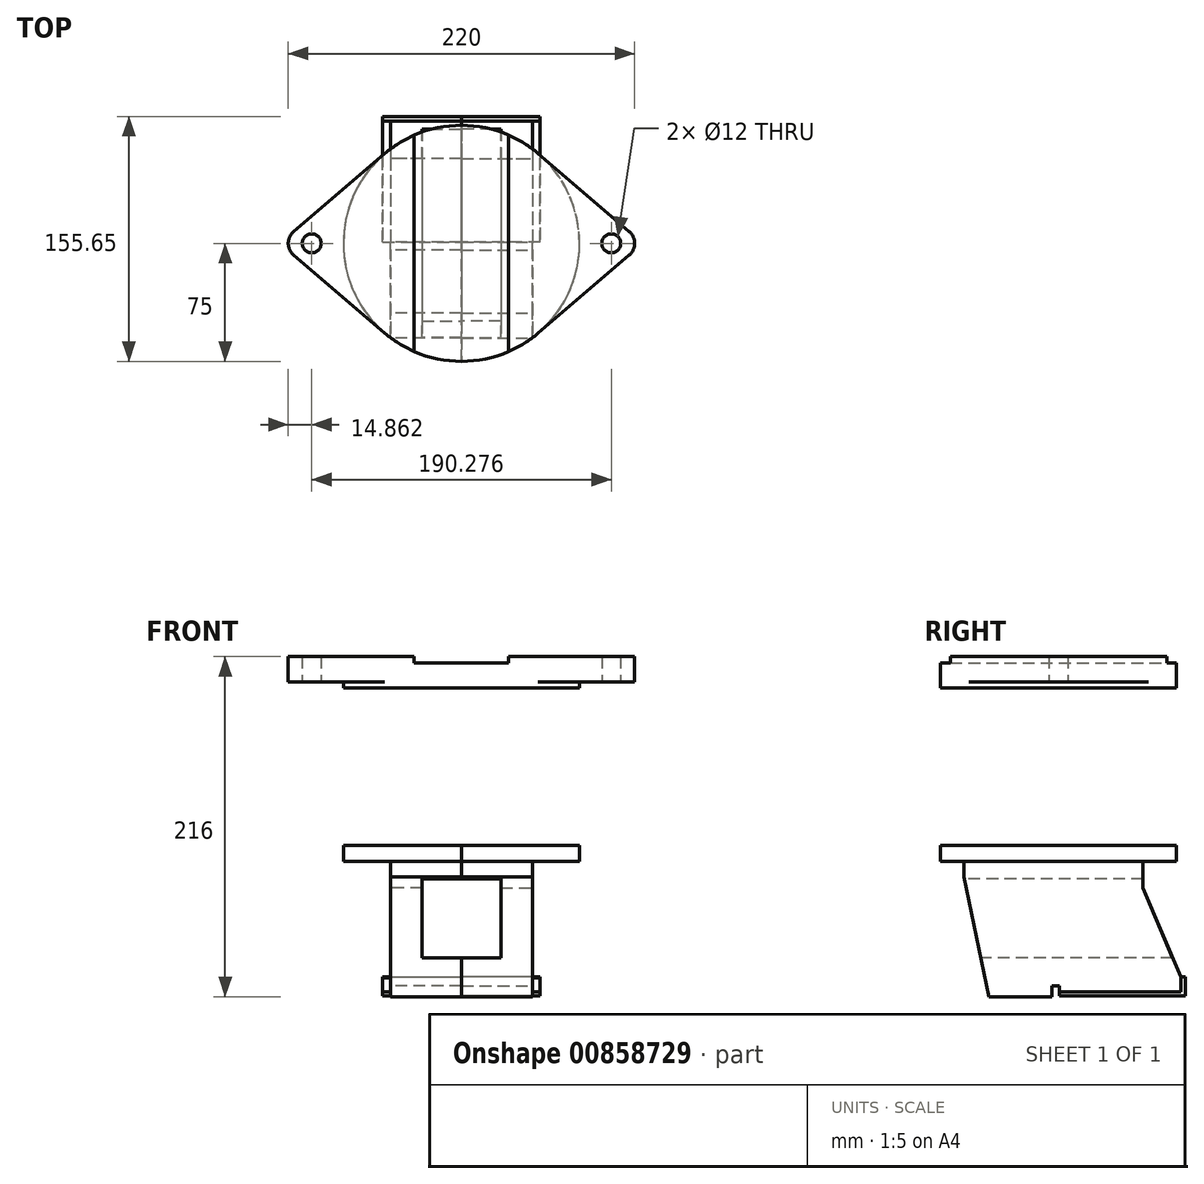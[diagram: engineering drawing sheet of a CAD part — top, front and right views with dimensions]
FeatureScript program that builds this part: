
annotation { "Feature Type Name" : "Feature", "Feature Type Description" : "" }
export const myFeature = defineFeature(function(context is Context, id is Id, definition is map)
    precondition{}
    {
        {
            var Q0;
            Q0=qCreatedBy(makeId("Top.planeOp"),FACE);
            var sketch = newSketch(context, id + "F0", { "sketchPlane" : qUnion([Q0])});
            skArc(sketch, "E0", {"start": v(0, 75) * mm, "mid": v(-25.99, 70.35) * mm, "end": v(-48.75, 57) * mm});
            skLineSegment(sketch, "E1", {"start": v(0, 0) * mm, "end": v(0, 0) * mm});
            skArc(sketch, "E2", {"start": v(-106.5, 7.6) * mm, "mid": v(-110, 0) * mm, "end": v(-106.5, -7.6) * mm});
            skLineSegment(sketch, "E3", {"start": v(-106.5, -7.6) * mm, "end": v(-48.75, -57) * mm});
            skLineSegment(sketch, "E4", {"start": v(-48.75, 57) * mm, "end": v(-106.5, 7.6) * mm});
            skArc(sketch, "E5.trimOffspring", {"start": v(-48.75, -57) * mm, "mid": v(-25.99, -70.35) * mm, "end": v(0, -75) * mm});
            skArc(sketch, "E6", {"start": v(0, 75) * mm, "mid": v(-75, 0) * mm, "end": v(0, -75) * mm});
            skLineSegment(sketch, "E7", {"start": v(0, 104.02) * mm, "end": v(0, -91.19) * mm});
            skSolve(sketch);
        }
        {
            var Q0;
            Q0=makeQuery(id+"F0.imprint","IMPRINT",FACE,{"disambiguationData":[TD([[makeQuery(id+"F0.imprint","IMPRINT",EDGE,{"derivedFrom":sQuery(id+"F0.wireOp",EDGE,"E2")}),1.0]])]});
            extrude(context, id + "F1", {"entities" : qUnion([Q0]), "oppositeDirection" : true, "depth" : 16 * mm, "offsetDistance" : 25 * mm});
        }
        {
            var Q0;
            {var subQ0=sQuery(id+"F0.wireOp",EDGE,"E6");var subQ1=makeQuery(id+"F0.imprint","INTERSECT",VERTEX,{"derivedFrom":[sQuery(id+"F0.wireOp",EDGE,"E4"),subQ0]});Q0=makeQuery(id+"F0.imprint","IMPRINT",FACE,{"disambiguationData":[TD([[makeQuery(id+"F0.imprint","IMPRINT",EDGE,{"disambiguationData":[TD([[subQ1,1.0]])],"derivedFrom":subQ0}),1.0]])]});}
            extrude(context, id + "F2", {"entities" : qUnion([Q0]), "oppositeDirection" : true, "depth" : 20 * mm, "offsetDistance" : 25 * mm});
        }
        {
            var Q0;
            Q0=makeQuery(id+"F1.opExtrude","CAP_FACE",FACE,{"disambiguationData":[OSD([sQuery(id+"F0.wireOp",EDGE,"E2"),sQuery(id+"F0.wireOp",EDGE,"E3"),sQuery(id+"F0.wireOp",EDGE,"E4"),sQuery(id+"F0.wireOp",EDGE,"E6")])],"isStart":false});
            var sketch = newSketch(context, id + "F3", { "sketchPlane" : qUnion([Q0])});
            skCircle(sketch, "E8", {"center": v(-95.14, 0) * mm, "radius": 6 * mm});
            skSolve(sketch);
        }
        {
            var Q0;
            Q0=makeQuery(id+"F3.imprint","IMPRINT",FACE,{"disambiguationData":[TD([[makeQuery(id+"F3.imprint","IMPRINT",EDGE,{"derivedFrom":sQuery(id+"F3.wireOp",EDGE,"E8")}),1.0]])]});
            extrude(context, id + "F4", {"entities" : qUnion([Q0]), "operationType" : NewBodyOperationType.REMOVE, "oppositeDirection" : true, "depth" : 16 * mm, "offsetDistance" : 25 * mm});
        }
        {
            var Q0;
            Q0=qCreatedBy(makeId("Front.planeOp"),FACE);
            var sketch = newSketch(context, id + "F5", { "sketchPlane" : qUnion([Q0])});
            skLineSegment(sketch, "E9", {"start": v(0, 0) * mm, "end": v(-30, 0) * mm});
            skLineSegment(sketch, "E10", {"start": v(-30, 0) * mm, "end": v(-30, -4) * mm});
            skLineSegment(sketch, "E11", {"start": v(-30, -4) * mm, "end": v(0, -4) * mm});
            skLineSegment(sketch, "E12", {"start": v(0, -4) * mm, "end": v(0, 0) * mm});
            skSolve(sketch);
        }
        {
            var Q0;
            Q0 = qSketchRegion(id + "F5", true);
            extrude(context, id + "F6", {"entities" : qUnion([Q0]), "operationType" : NewBodyOperationType.REMOVE, "endBound" : BoundingType.SYMMETRIC, "depth" : 150 * mm, "offsetDistance" : 25 * mm});
        }
        {
            var Q0;
            Q0=makeQuery(id+"F1.opExtrude","SWEPT_BODY",BODY,{"disambiguationData":[OSD([sQuery(id+"F0.wireOp",EDGE,"E2"),sQuery(id+"F0.wireOp",EDGE,"E3"),sQuery(id+"F0.wireOp",EDGE,"E4"),sQuery(id+"F0.wireOp",EDGE,"E6")])]});
            var Q1;
            Q1=makeQuery(id+"F2.opExtrude","SWEPT_BODY",BODY,{"disambiguationData":[OSD([sQuery(id+"F0.wireOp",EDGE,"E6"),sQuery(id+"F0.wireOp",EDGE,"E7")])]});
            var Q2;
            Q2=makeQuery(id+"F2.opExtrude","SWEPT_FACE",FACE,{"disambiguationData":[OSD([sQuery(id+"F0.wireOp",EDGE,"E7")])]});
            mirror(context, id + "F7", {"operationType" : NewBodyOperationType.ADD, "entities" : qUnion([Q0, Q1]), "mirrorPlane" : qUnion([Q2])});
        }
        {
            var Q0;
            {var subQ0=makeQuery(id+"F2.opExtrude","CAP_FACE",FACE,{"disambiguationData":[OSD([sQuery(id+"F0.wireOp",EDGE,"E6"),sQuery(id+"F0.wireOp",EDGE,"E7")])],"isStart":false});Q0=makeQuery(id+"F7.boolean.opBoolean","MERGE",FACE,{"derivedFrom":[subQ0,makeQuery(id+"F7.opPattern","COPY",FACE,{"derivedFrom":subQ0,"instanceName":"1"})]});}
            var sketch = newSketch(context, id + "F8", { "sketchPlane" : qUnion([Q0])});
            skCircle(sketch, "E13", {"center": v(0, 0) * mm, "radius": 75 * mm});
            skSolve(sketch);
        }
        {
            var Q0;
            Q0 = qSketchRegion(id + "F8", true);
            var Q1;
            {var subQ0=makeQuery(id+"F2.opExtrude","CAP_FACE",FACE,{"disambiguationData":[OSD([sQuery(id+"F0.wireOp",EDGE,"E6"),sQuery(id+"F0.wireOp",EDGE,"E7")])],"isStart":false});Q1=makeQuery(id+"F7.boolean.opBoolean","MERGE",FACE,{"derivedFrom":[subQ0,makeQuery(id+"F7.opPattern","COPY",FACE,{"derivedFrom":subQ0,"instanceName":"1"})]});}
            extrude(context, id + "F9", {"entities" : qUnion([Q0]), "depth" : 10 * mm, "endBoundEntityFace" : qUnion([Q1]), "offsetDistance" : 25 * mm});
        }
        {
            var Q0;
            Q0=makeQuery(id+"F9.opExtrude","SWEPT_BODY",BODY,{"disambiguationData":[OSD([sQuery(id+"F8.wireOp",EDGE,"E13")])]});
            transform(context, id + "F10", {"entities" : qUnion([Q0]), "transformType" : TransformType.TRANSLATION_3D, "dx" : 0 * mm, "dy" : 0 * mm, "dz" : -100 * mm, "makeCopy" : false});
        }
        {
            var Q0;
            Q0=qCreatedBy(makeId("Front.planeOp"),FACE);
            var sketch = newSketch(context, id + "F11", { "sketchPlane" : qUnion([Q0])});
            skLineSegment(sketch, "E14", {"start": v(-45, -126) * mm, "end": v(45, -126) * mm});
            skLineSegment(sketch, "E15", {"start": v(45, -126) * mm, "end": v(45, -216) * mm});
            skLineSegment(sketch, "E16", {"start": v(-45, -126) * mm, "end": v(-45, -216) * mm});
            skPoint(sketch, "E17.start.orphan", {"position": v(0, -126) * mm});
            skLineSegment(sketch, "E18", {"start": v(45, -216) * mm, "end": v(-45, -216) * mm});
            skLineSegment(sketch, "E19", {"start": v(0, -126) * mm, "end": v(0, 0) * mm});
            skSolve(sketch);
        }
        {
            var Q0;
            Q0=makeQuery(id+"F11.imprint","IMPRINT",FACE,{"disambiguationData":[TD([[makeQuery(id+"F11.imprint","IMPRINT",EDGE,{"derivedFrom":sQuery(id+"F11.wireOp",EDGE,"E14")}),-1.0]])]});
            extrude(context, id + "F12", {"entities" : qUnion([Q0]), "operationType" : NewBodyOperationType.ADD, "depth" : 60 * mm, "offsetDistance" : 25 * mm});
        }
        {
            var Q0;
            Q0=makeQuery(id+"F12.opExtrude","CAP_FACE",FACE,{"disambiguationData":[OSD([sQuery(id+"F11.wireOp",EDGE,"E14"),sQuery(id+"F11.wireOp",EDGE,"E15"),sQuery(id+"F11.wireOp",EDGE,"E16"),sQuery(id+"F11.wireOp",EDGE,"E18")])],"isStart":true});
            extrude(context, id + "F13", {"entities" : qUnion([Q0]), "operationType" : NewBodyOperationType.ADD, "depth" : 77.8 * mm, "offsetDistance" : 25 * mm});
        }
        {
            var Q0;
            Q0=makeQuery(id+"F9.opExtrude","CAP_FACE",FACE,{"disambiguationData":[OSD([sQuery(id+"F8.wireOp",EDGE,"E13")])],"isStart":true});
            var sketch = newSketch(context, id + "F14", { "sketchPlane" : qUnion([Q0])});
            skLineSegment(sketch, "E20", {"start": v(0, -75) * mm, "end": v(0, 95.24) * mm});
            skLineSegment(sketch, "E21", {"start": v(0, 95.24) * mm, "end": v(93.31, 95.24) * mm});
            skLineSegment(sketch, "E22", {"start": v(93.31, 95.24) * mm, "end": v(93.31, -75) * mm});
            skLineSegment(sketch, "E23", {"start": v(93.31, -75) * mm, "end": v(0, -75) * mm});
            skSolve(sketch);
        }
        {
            var Q0;
            {var subQ1=sQuery(id+"F14.wireOp",EDGE,"E21");Q0=makeQuery(id+"F14.imprint","IMPRINT",FACE,{"disambiguationData":[TD([[makeQuery(id+"F14.imprint","IMPRINT",EDGE,{"derivedFrom":subQ1}),-1.0]])]});}
            var Q1;
            {var subQ0=sQuery(id+"F14.wireOp",EDGE,"E20");var subQ1=makeQuery(id+"F9.opExtrude","CAP_EDGE",EDGE,{"disambiguationData":[OSD([sQuery(id+"F8.wireOp",EDGE,"E13")])],"isStart":true});var subQ3=makeQuery(id+"F14.imprint","INTERSECT",VERTEX,{"derivedFrom":[subQ1,subQ0]});Q1=makeQuery(id+"F14.imprint","IMPRINT",FACE,{"disambiguationData":[TD([[makeQuery(id+"F14.imprint","IMPRINT",EDGE,{"disambiguationData":[TD([[subQ3,1.0]])],"derivedFrom":subQ0}),-1.0]])]});}
            extrude(context, id + "F15", {"entities" : qUnion([Q0, Q1]), "operationType" : NewBodyOperationType.REMOVE, "oppositeDirection" : true, "depth" : 100 * mm, "offsetDistance" : 25 * mm});
        }
        {
            var Q0;
            {var subQ0=sQuery(id+"F11.wireOp",EDGE,"E16");Q0=makeQuery(id+"F13.boolean.opBoolean","MERGE",FACE,{"derivedFrom":[makeQuery(id+"F12.opExtrude","SWEPT_FACE",FACE,{"disambiguationData":[OSD([subQ0])]}),makeQuery(id+"F13.opExtrude","SWEPT_FACE",FACE,{"disambiguationData":[OSD([subQ0])]})]});}
            var sketch = newSketch(context, id + "F16", { "sketchPlane" : qUnion([Q0])});
            skLineSegment(sketch, "E24", {"start": v(60, -130) * mm, "end": v(60, -140) * mm});
            skLineSegment(sketch, "E25", {"start": v(60, -140) * mm, "end": v(44.35, -216) * mm});
            skLineSegment(sketch, "E26", {"start": v(44.35, -216) * mm, "end": v(4.35, -216) * mm});
            skLineSegment(sketch, "E27", {"start": v(4.35, -216) * mm, "end": v(4.35, -213) * mm});
            skLineSegment(sketch, "E28", {"start": v(-0.65, -213) * mm, "end": v(-0.65, -216) * mm});
            skLineSegment(sketch, "E29", {"start": v(-0.65, -216) * mm, "end": v(-83.5, -216) * mm});
            skLineSegment(sketch, "E30", {"start": v(-77.8, -216) * mm, "end": v(-77.8, -204) * mm});
            skLineSegment(sketch, "E31", {"start": v(-77.8, -204) * mm, "end": v(-53.7, -146.88) * mm});
            skLineSegment(sketch, "E32", {"start": v(-77.8, -130) * mm, "end": v(-77.8, -204) * mm});
            skLineSegment(sketch, "E33", {"start": v(4.35, -213) * mm, "end": v(4.35, -209) * mm});
            skLineSegment(sketch, "E34", {"start": v(4.35, -209) * mm, "end": v(-0.65, -209) * mm});
            skLineSegment(sketch, "E35", {"start": v(-0.65, -209) * mm, "end": v(-0.65, -213) * mm});
            skLineSegment(sketch, "E36", {"start": v(-77.8, -213) * mm, "end": v(-0.65, -213) * mm});
            skLineSegment(sketch, "E37", {"start": v(-53.7, -146.88) * mm, "end": v(-53.7, -130) * mm});
            skLineSegment(sketch, "E38", {"start": v(-53.7, -130) * mm, "end": v(-77.8, -130) * mm});
            skSolve(sketch);
        }
        {
            var Q0;
            Q0 = qSketchRegion(id + "F16", true);
            var Q1;
            {var subQ0=sQuery(id+"F16.wireOp",EDGE,"E25");Q1=makeQuery(id+"F16.imprint","IMPRINT",FACE,{"disambiguationData":[TD([[makeQuery(id+"F16.imprint","IMPRINT",EDGE,{"derivedFrom":subQ0}),1.0]])]});}
            var Q2;
            {var subQ0=sQuery(id+"F16.wireOp",EDGE,"E27");Q2=makeQuery(id+"F16.imprint","IMPRINT",FACE,{"disambiguationData":[TD([[makeQuery(id+"F16.imprint","IMPRINT",EDGE,{"derivedFrom":subQ0}),1.0]])]});}
            extrude(context, id + "F17", {"entities" : qUnion([Q0, Q1, Q2]), "operationType" : NewBodyOperationType.REMOVE, "oppositeDirection" : true, "depth" : 45 * mm, "offsetDistance" : 25 * mm});
        }
        {
            var Q0;
            Q0=makeQuery(id+"F15.boolean.opBoolean","COPY",FACE,{"derivedFrom":makeQuery(id+"F15.opExtrude","SWEPT_FACE",FACE,{"disambiguationData":[OSD([sQuery(id+"F14.wireOp",EDGE,"E20")])]})});
            var sketch = newSketch(context, id + "F18", { "sketchPlane" : qUnion([Q0])});
            skLineSegment(sketch, "E39.top", {"start": v(77.8, -203.48) * mm, "end": v(0.65, -203.48) * mm});
            skLineSegment(sketch, "E40", {"start": v(0.65, -203.48) * mm, "end": v(0.65, -215.48) * mm});
            skLineSegment(sketch, "E41", {"start": v(0.65, -215.48) * mm, "end": v(80.65, -215.48) * mm});
            skLineSegment(sketch, "E42", {"start": v(80.65, -215.48) * mm, "end": v(80.65, -203.48) * mm});
            skLineSegment(sketch, "E43", {"start": v(80.65, -203.48) * mm, "end": v(77.8, -203.48) * mm});
            skSolve(sketch);
        }
        {
            var Q0;
            {var subQ2=sQuery(id+"F18.wireOp",EDGE,"E41");Q0=makeQuery(id+"F18.imprint","IMPRINT",FACE,{"disambiguationData":[TD([[makeQuery(id+"F18.imprint","IMPRINT",EDGE,{"derivedFrom":subQ2}),1.0]])]});}
            var Q1;
            {var subQ0=makeQuery(id+"F17.boolean.opBoolean","COPY",EDGE,{"derivedFrom":makeQuery(id+"F17.opExtrude","CAP_EDGE",EDGE,{"disambiguationData":[OSD([sQuery(id+"F16.wireOp",EDGE,"E36")])],"isStart":false})});Q1=makeQuery(id+"F18.imprint","IMPRINT",FACE,{"disambiguationData":[TD([[makeQuery(id+"F18.imprint","IMPRINT",EDGE,{"derivedFrom":subQ0}),-1.0]])]});}
            extrude(context, id + "F19", {"entities" : qUnion([Q0, Q1]), "operationType" : NewBodyOperationType.ADD, "oppositeDirection" : true, "depth" : 50 * mm, "offsetDistance" : 25 * mm});
        }
        {
            var Q0;
            Q0=qCreatedBy(makeId("Front.planeOp"),FACE);
            var sketch = newSketch(context, id + "F20", { "sketchPlane" : qUnion([Q0])});
            skLineSegment(sketch, "E44", {"start": v(0, -131.23) * mm, "end": v(0, -141.23) * mm});
            skLineSegment(sketch, "E45", {"start": v(0, -141.23) * mm, "end": v(-25, -141.23) * mm});
            skLineSegment(sketch, "E46", {"start": v(-25, -141.23) * mm, "end": v(-25, -191.23) * mm});
            skLineSegment(sketch, "E47", {"start": v(-25, -191.23) * mm, "end": v(0, -191.23) * mm});
            skLineSegment(sketch, "E48", {"start": v(0, -191.23) * mm, "end": v(0, -141.23) * mm});
            skSolve(sketch);
        }
        {
            var Q0;
            Q0 = qSketchRegion(id + "F20", true);
            extrude(context, id + "F21", {"entities" : qUnion([Q0]), "operationType" : NewBodyOperationType.REMOVE, "oppositeDirection" : true, "depth" : 80 * mm, "offsetDistance" : 25 * mm});
        }
        {
            var Q0;
            Q0=makeQuery(id+"F21.boolean.opBoolean","COPY",FACE,{"derivedFrom":makeQuery(id+"F21.opExtrude","CAP_FACE",FACE,{"disambiguationData":[OSD([sQuery(id+"F20.wireOp",EDGE,"E45"),sQuery(id+"F20.wireOp",EDGE,"E46"),sQuery(id+"F20.wireOp",EDGE,"E47"),sQuery(id+"F20.wireOp",EDGE,"E48")])],"isStart":true})});
            extrude(context, id + "F22", {"entities" : qUnion([Q0]), "operationType" : NewBodyOperationType.REMOVE, "oppositeDirection" : true, "depth" : 80 * mm, "offsetDistance" : 25 * mm});
        }
        {
            var Q0;
            Q0=makeQuery(id+"F9.opExtrude","SWEPT_BODY",BODY,{"disambiguationData":[OSD([sQuery(id+"F8.wireOp",EDGE,"E13")])]});
            var Q1;
            {var subQ0=sQuery(id+"F18.wireOp",EDGE,"E40");var subQ1=sQuery(id+"F18.wireOp",EDGE,"E43");var subQ2=sQuery(id+"F18.wireOp",EDGE,"E39.top");var subQ4=sQuery(id+"F18.wireOp",EDGE,"E41");var subQ5=sQuery(id+"F11.wireOp",EDGE,"E18");var subQ6=sQuery(id+"F18.wireOp",EDGE,"E42");Q1=makeQuery(id+"F22.boolean.opBoolean","SPLIT",FACE,{"disambiguationData":[TD([makeQuery(id+"F12.opExtrude","SWEPT_FACE",FACE,{"disambiguationData":[OSD([subQ5])]})])],"derivedFrom":makeQuery(id+"F19.boolean.opBoolean","MERGE",FACE,{"derivedFrom":[makeQuery(id+"F15.boolean.opBoolean","COPY",FACE,{"derivedFrom":makeQuery(id+"F15.opExtrude","SWEPT_FACE",FACE,{"disambiguationData":[OSD([sQuery(id+"F14.wireOp",EDGE,"E20")])]})}),makeQuery(id+"F19.opExtrude","CAP_FACE",FACE,{"disambiguationData":[OSD([subQ2,subQ0,subQ4,subQ6,subQ1])],"isStart":true})]})});}
            mirror(context, id + "F23", {"operationType" : NewBodyOperationType.ADD, "entities" : qUnion([Q0]), "mirrorPlane" : qUnion([Q1])});
        }
    });
